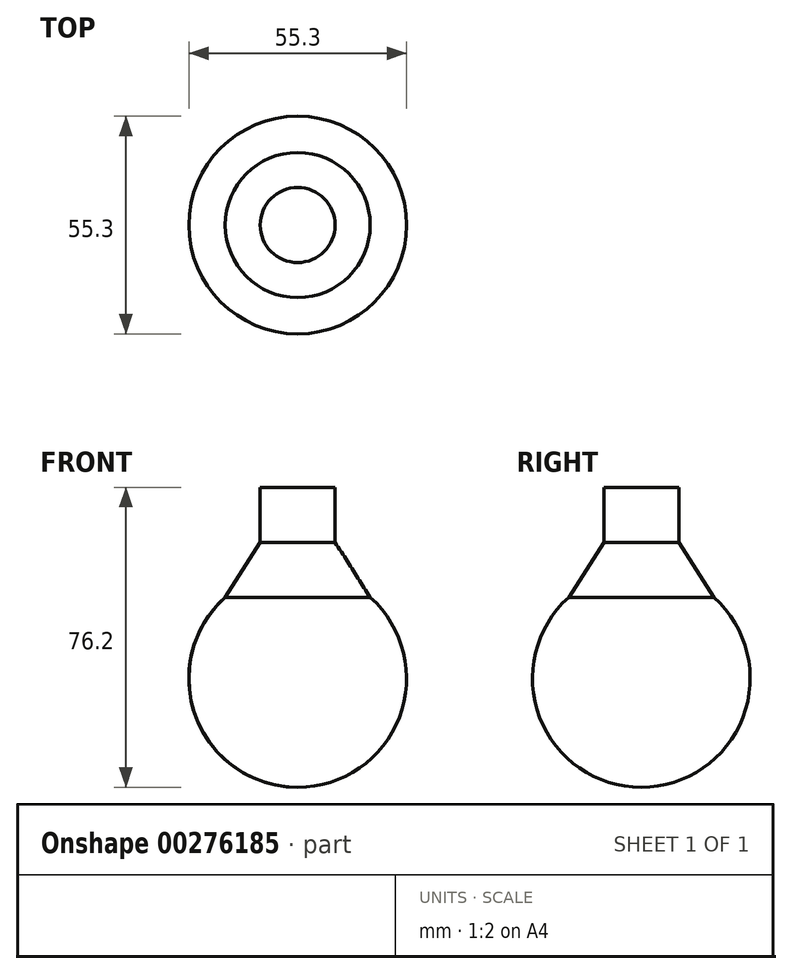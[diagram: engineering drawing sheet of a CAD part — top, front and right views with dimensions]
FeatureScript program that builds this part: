
annotation { "Feature Type Name" : "Feature", "Feature Type Description" : "" }
export const myFeature = defineFeature(function(context is Context, id is Id, definition is map)
    precondition{}
    {
        {
            var Q0;
            Q0=qCreatedBy(makeId("Front.planeOp"),FACE);
            var sketch = newSketch(context, id + "F0", { "sketchPlane" : qUnion([Q0])});
            skLineSegment(sketch, "E0", {"start": v(0, 0) * mm, "end": v(9.52, 0) * mm});
            skLineSegment(sketch, "E1", {"start": v(9.52, 0) * mm, "end": v(9.53, -13.97) * mm});
            skLineSegment(sketch, "E2", {"start": v(0, -13.97) * mm, "end": v(0, 0) * mm});
            skLineSegment(sketch, "E3", {"start": v(9.53, -13.97) * mm, "end": v(18.44, -27.94) * mm});
            skArc(sketch, "E4", {"start": v(0, -76.2) * mm, "mid": v(25.83, -58.42) * mm, "end": v(18.44, -27.94) * mm});
            skLineSegment(sketch, "E5", {"start": v(0, -13.97) * mm, "end": v(0, -76.2) * mm});
            skSolve(sketch);
        }
        {
            var Q0;
            Q0 = qSketchRegion(id + "F0", true);
            var Q1;
            Q1=sQuery(id+"F0.wireOp",EDGE,"E5");
            revolve(context, id + "F1", {"entities" : qUnion([Q0]), "axis" : qUnion([Q1]), "revolveType" : RevolveType.FULL});
        }
    });
